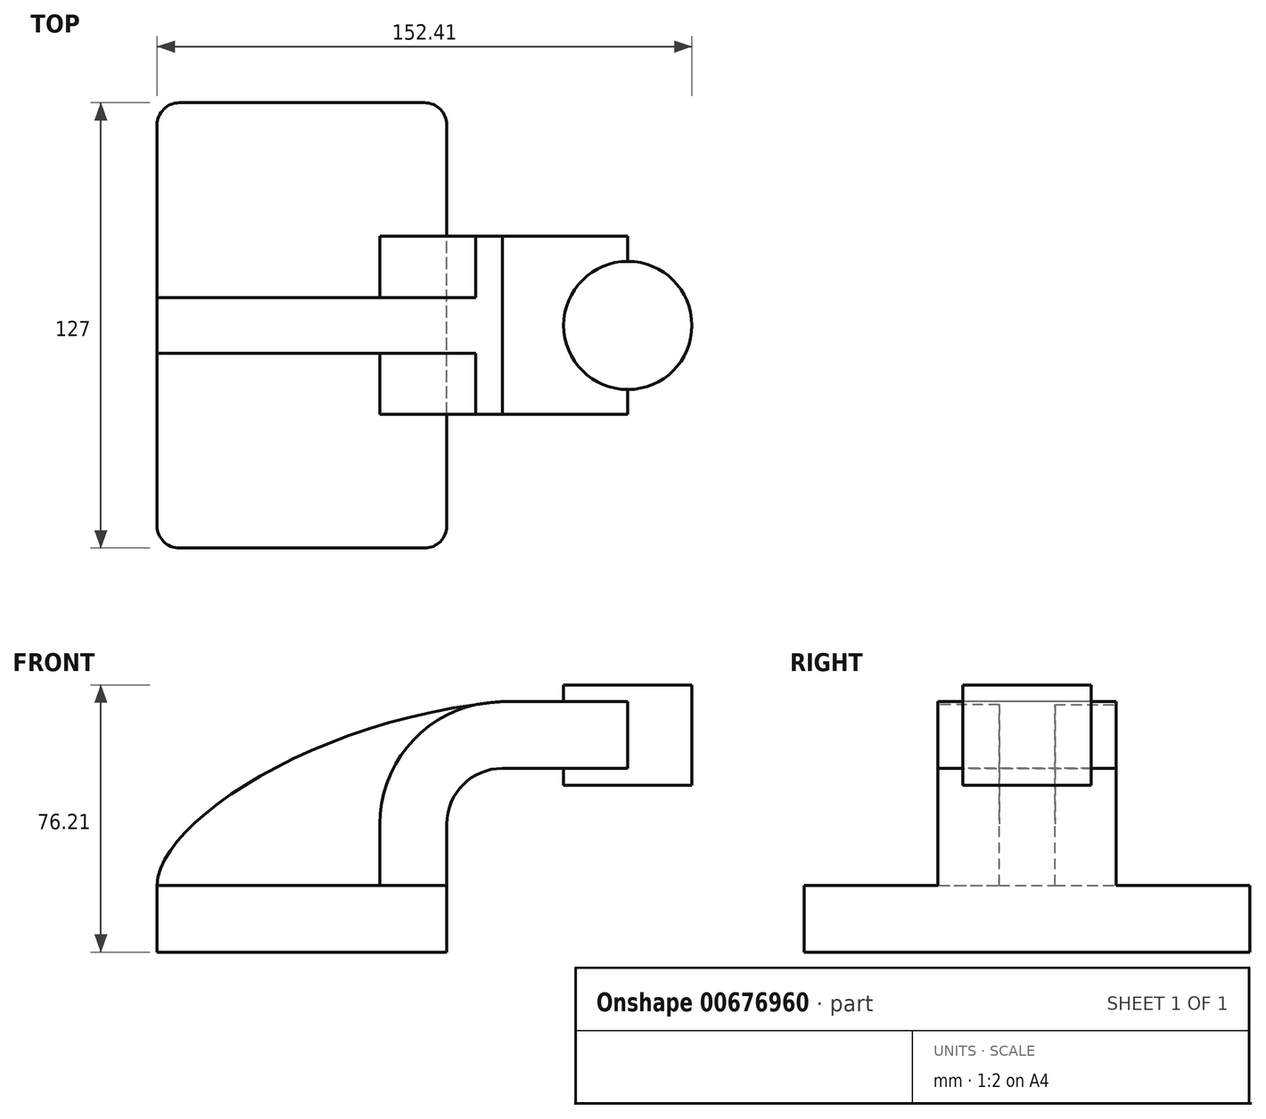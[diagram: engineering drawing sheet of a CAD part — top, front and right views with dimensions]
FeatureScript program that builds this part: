
annotation { "Feature Type Name" : "Feature", "Feature Type Description" : "" }
export const myFeature = defineFeature(function(context is Context, id is Id, definition is map)
    precondition{}
    {
        {
            var Q0;
            Q0=qCreatedBy(makeId("Front.planeOp"),FACE);
            var sketch = newSketch(context, id + "F0", { "sketchPlane" : qUnion([Q0])});
            skLineSegment(sketch, "E0.bottom", {"start": v(-41.28, -9.53) * mm, "end": v(41.27, -9.53) * mm});
            skLineSegment(sketch, "E0.top", {"start": v(-41.28, 9.53) * mm, "end": v(41.27, 9.53) * mm});
            skLineSegment(sketch, "E0.left", {"start": v(-41.28, -9.53) * mm, "end": v(-41.28, 9.53) * mm});
            skLineSegment(sketch, "E0.right", {"start": v(41.27, -9.53) * mm, "end": v(41.27, 9.53) * mm});
            skPoint(sketch, "E0.middle", {"position": v(0, 0) * mm});
            skLineSegment(sketch, "E1.bottom", {"start": v(60.32, 38.1) * mm, "end": v(111.13, 38.1) * mm});
            skLineSegment(sketch, "E1.top", {"start": v(60.32, 66.67) * mm, "end": v(111.13, 66.67) * mm});
            skLineSegment(sketch, "E1.left", {"start": v(60.32, 38.1) * mm, "end": v(60.32, 66.68) * mm});
            skLineSegment(sketch, "E1.right", {"start": v(111.13, 38.1) * mm, "end": v(111.13, 66.68) * mm});
            skPoint(sketch, "E1.middle", {"position": v(85.73, 52.39) * mm});
            skLineSegment(sketch, "E2", {"start": v(41.27, 9.53) * mm, "end": v(41.27, 27) * mm});
            skArc(sketch, "E3", {"start": v(41.27, 27) * mm, "mid": v(45.92, 38.23) * mm, "end": v(57.15, 42.88) * mm});
            skLineSegment(sketch, "E4", {"start": v(57.15, 42.88) * mm, "end": v(92.84, 42.88) * mm});
            skLineSegment(sketch, "E5.0", {"start": v(57.15, 61.93) * mm, "end": v(92.84, 61.93) * mm});
            skArc(sketch, "E5.1", {"start": v(22.22, 27) * mm, "mid": v(32.45, 51.7) * mm, "end": v(57.15, 61.93) * mm});
            skLineSegment(sketch, "E5.2", {"start": v(22.22, 9.53) * mm, "end": v(22.22, 27) * mm});
            skLineSegment(sketch, "E6", {"start": v(92.84, 42.88) * mm, "end": v(92.84, 61.93) * mm});
            skFitSpline(sketch, "E7", {"points": [v(-41.28, 9.53) * mm, v(57.15, 61.93) * mm], "startDerivative": vector(0.9, 54.94) * mm, "endDerivative": vector(155.63, 13.46) * mm});
            skLineSegment(sketch, "E8", {"start": v(92.84, 61.93) * mm, "end": v(92.84, 66.67) * mm});
            skLineSegment(sketch, "E9", {"start": v(92.84, 42.88) * mm, "end": v(92.84, 38.1) * mm});
            skSolve(sketch);
        }
        {
            var Q0;
            Q0=makeQuery(id+"F0.imprint","IMPRINT",FACE,{"disambiguationData":[TD([[makeQuery(id+"F0.imprint","IMPRINT",EDGE,{"derivedFrom":sQuery(id+"F0.wireOp",EDGE,"E0.bottom")}),1.0]])]});
            extrude(context, id + "F1", {"entities" : qUnion([Q0]), "endBound" : BoundingType.SYMMETRIC, "depth" : 127 * mm, "offsetDistance" : 25.4 * mm});
        }
        {
            var Q0;
            {var subQ0=sQuery(id+"F0.wireOp",EDGE,"E2");Q0=makeQuery(id+"F0.imprint","IMPRINT",FACE,{"disambiguationData":[TD([[makeQuery(id+"F0.imprint","IMPRINT",EDGE,{"derivedFrom":subQ0}),1.0]])]});}
            var Q1;
            {var subQ5=sQuery(id+"F0.wireOp",EDGE,"E6");Q1=makeQuery(id+"F0.imprint","IMPRINT",FACE,{"disambiguationData":[TD([[makeQuery(id+"F0.imprint","IMPRINT",EDGE,{"derivedFrom":subQ5}),1.0]])]});}
            extrude(context, id + "F2", {"entities" : qUnion([Q0, Q1]), "operationType" : NewBodyOperationType.ADD, "endBound" : BoundingType.SYMMETRIC, "depth" : 50.8 * mm, "offsetDistance" : 25.4 * mm});
        }
        {
            var Q0;
            {var subQ3=sQuery(id+"F0.wireOp",EDGE,"E5.2");Q0=makeQuery(id+"F0.imprint","IMPRINT",FACE,{"disambiguationData":[TD([[makeQuery(id+"F0.imprint","IMPRINT",EDGE,{"derivedFrom":subQ3}),1.0]])]});}
            extrude(context, id + "F3", {"entities" : qUnion([Q0]), "operationType" : NewBodyOperationType.ADD, "endBound" : BoundingType.SYMMETRIC, "depth" : 15.88 * mm, "offsetDistance" : 25.4 * mm});
        }
        {
            var Q0;
            {var subQ0=sQuery(id+"F0.wireOp",EDGE,"E1.right");Q0=makeQuery(id+"F0.imprint","IMPRINT",FACE,{"disambiguationData":[TD([[makeQuery(id+"F0.imprint","IMPRINT",EDGE,{"derivedFrom":subQ0}),1.0]])]});}
            var Q1;
            Q1=sQuery(id+"F0.wireOp",EDGE,"E6");
            revolve(context, id + "F4", {"operationType" : NewBodyOperationType.ADD, "entities" : qUnion([Q0]), "axis" : qUnion([Q1]), "revolveType" : RevolveType.FULL});
        }
        {
            var Q0;
            Q0=makeQuery(id+"F1.opExtrude","CAP_EDGE",EDGE,{"disambiguationData":[OSD([sQuery(id+"F0.wireOp",EDGE,"E0.right")])],"isStart":false});
            var Q1;
            Q1=makeQuery(id+"F1.opExtrude","CAP_EDGE",EDGE,{"disambiguationData":[OSD([sQuery(id+"F0.wireOp",EDGE,"E0.left")])],"isStart":false});
            var Q2;
            Q2=makeQuery(id+"F1.opExtrude","CAP_EDGE",EDGE,{"disambiguationData":[OSD([sQuery(id+"F0.wireOp",EDGE,"E0.left")])],"isStart":true});
            var Q3;
            Q3=makeQuery(id+"F1.opExtrude","CAP_EDGE",EDGE,{"disambiguationData":[OSD([sQuery(id+"F0.wireOp",EDGE,"E0.right")])],"isStart":true});
            fillet(context, id + "F5", {"entities" : qUnion([Q0, Q1, Q2, Q3]), "radius" : 6.35 * mm, "tangentPropagation" : true, "allowEdgeOverflow" : false});
        }
    });
